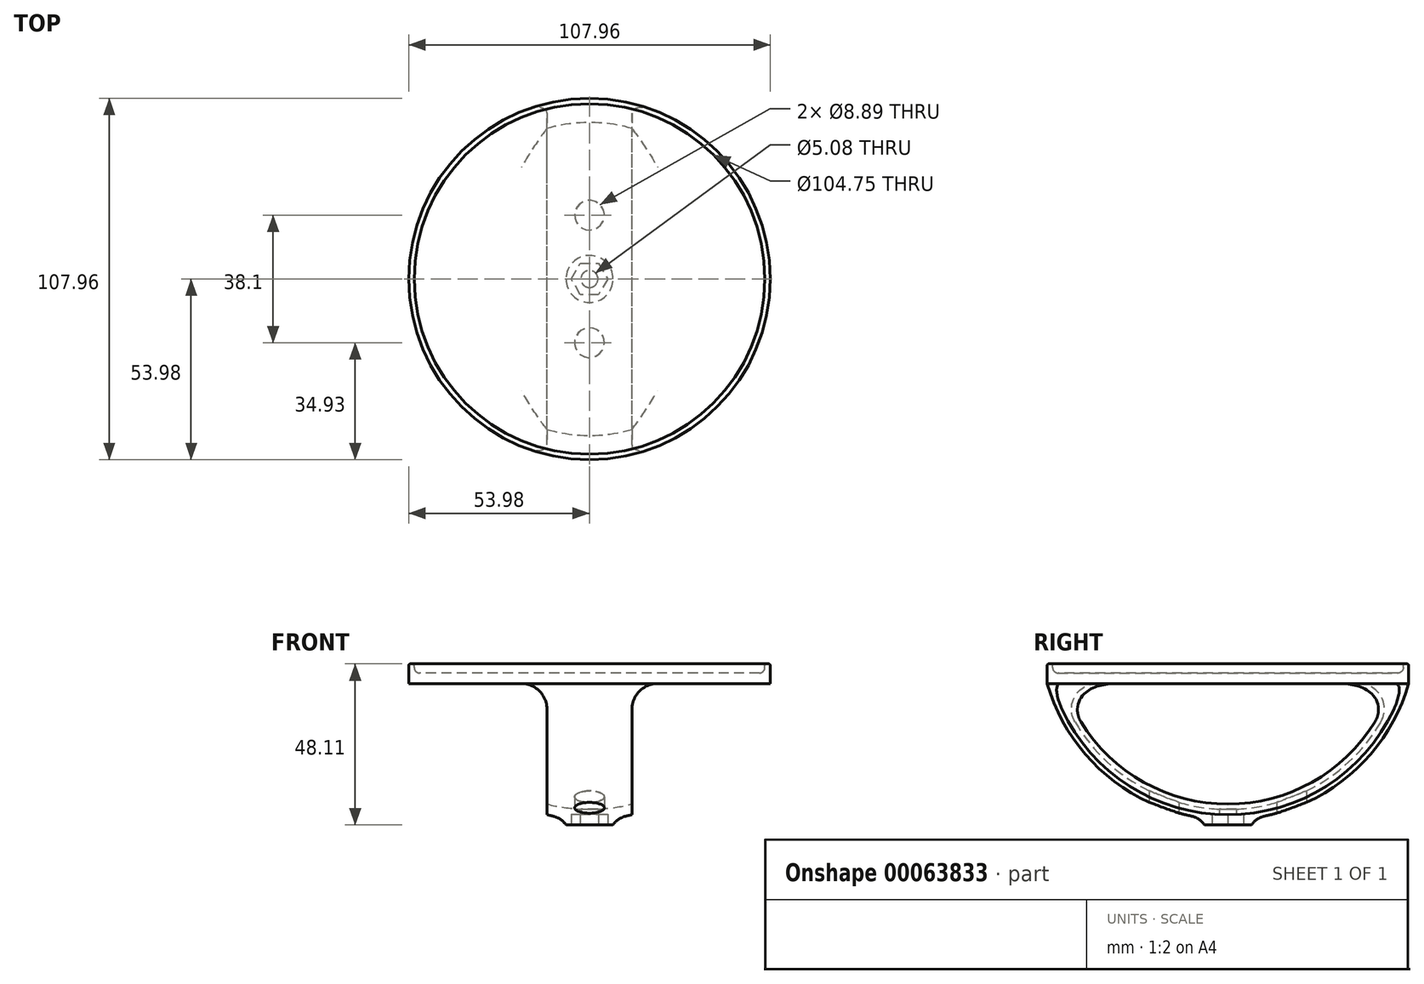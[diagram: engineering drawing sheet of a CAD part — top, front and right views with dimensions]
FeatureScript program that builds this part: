
annotation { "Feature Type Name" : "Feature", "Feature Type Description" : "" }
export const myFeature = defineFeature(function(context is Context, id is Id, definition is map)
    precondition{}
    {
        {
            var Q0;
            Q0=qCreatedBy(makeId("Front.planeOp"),FACE);
            var sketch = newSketch(context, id + "F0", { "sketchPlane" : qUnion([Q0])});
            skLineSegment(sketch, "E0", {"start": v(0, 0) * mm, "end": v(-50.74, 0) * mm});
            skLineSegment(sketch, "E1", {"start": v(-50.77, 3.17) * mm, "end": v(0, 3.17) * mm});
            skLineSegment(sketch, "E2", {"start": v(0, 0) * mm, "end": v(0, 3.17) * mm});
            skLineSegment(sketch, "E3", {"start": v(0, 3.17) * mm, "end": v(0, -13.72) * mm, "construction": true});
            skLineSegment(sketch, "E4", {"start": v(-53.98, 0) * mm, "end": v(-53.98, 5.4) * mm});
            skLineSegment(sketch, "E5", {"start": v(-53.47, 5.9) * mm, "end": v(-52.88, 5.9) * mm});
            skLineSegment(sketch, "E6", {"start": v(-52.37, 5.4) * mm, "end": v(-52.37, 4.78) * mm});
            skPoint(sketch, "E7.visualSharp", {"position": v(-52.37, 3.17) * mm});
            skArc(sketch, "E7.filletArc", {"start": v(-52.37, 4.78) * mm, "mid": v(-51.9, 3.64) * mm, "end": v(-50.77, 3.17) * mm});
            skPoint(sketch, "E8.visualSharp", {"position": v(-53.98, 5.9) * mm});
            skArc(sketch, "E8.filletArc", {"start": v(-53.47, 5.9) * mm, "mid": v(-53.83, 5.76) * mm, "end": v(-53.98, 5.4) * mm});
            skPoint(sketch, "E9.visualSharp", {"position": v(-52.37, 5.9) * mm});
            skArc(sketch, "E9.filletArc", {"start": v(-52.37, 5.4) * mm, "mid": v(-52.52, 5.76) * mm, "end": v(-52.88, 5.9) * mm});
            skArc(sketch, "E10", {"start": v(-53.97, 0) * mm, "mid": v(-33.78, -29.34) * mm, "end": v(0, -40.64) * mm});
            skArc(sketch, "E11", {"start": v(-50.74, 0) * mm, "mid": v(-31.56, -27.14) * mm, "end": v(0, -37.54) * mm});
            skLineSegment(sketch, "E12", {"start": v(0, -40.64) * mm, "end": v(0, -37.54) * mm});
            skSolve(sketch);
        }
        {
            var Q0;
            Q0=qSketchRegion(id+"F0",true);
            var Q1;
            Q1=sQuery(id+"F0.wireOp",EDGE,"E3");
            revolve(context, id + "F1", {"entities" : qUnion([Q0]), "axis" : qUnion([Q1]), "revolveType" : RevolveType.FULL});
        }
        {
            var Q0;
            Q0=qCreatedBy(makeId("Top.planeOp"),FACE);
            cPlane(context, id + "F2", {"entities" : qUnion([Q0]), "cplaneType" : CPlaneType.OFFSET, "offset" : 40.64 * mm, "oppositeDirection" : true, "width" : 152.4 * mm, "height" : 152.4 * mm});
        }
        {
            var Q0;
            Q0=qCreatedBy(id+"F2.planeOp",FACE);
            var sketch = newSketch(context, id + "F3", { "sketchPlane" : qUnion([Q0])});
            skLineSegment(sketch, "E13", {"start": v(-12.7, 65.77) * mm, "end": v(-12.7, -65.77) * mm});
            skArc(sketch, "E14", {"start": v(-12.7, 65.77) * mm, "mid": v(-66.99, 0) * mm, "end": v(-12.7, -65.77) * mm});
            skLineSegment(sketch, "E15", {"start": v(12.7, 65.77) * mm, "end": v(12.7, -65.77) * mm});
            skArc(sketch, "E16", {"start": v(12.7, -65.77) * mm, "mid": v(66.99, 0) * mm, "end": v(12.7, 65.77) * mm});
            skLineSegment(sketch, "E17", {"start": v(-12.7, 65.77) * mm, "end": v(12.7, 65.77) * mm, "construction": true});
            skPoint(sketch, "E18", {"position": v(0, 65.77) * mm});
            skCircle(sketch, "E19", {"center": v(0, 0) * mm, "radius": 2.54 * mm});
            skCircle(sketch, "E20", {"center": v(0, 19.05) * mm, "radius": 4.44 * mm});
            skCircle(sketch, "E21", {"center": v(0, -19.05) * mm, "radius": 4.44 * mm});
            skLineSegment(sketch, "E22", {"start": v(0, 0) * mm, "end": v(0, 19.05) * mm, "construction": true});
            skLineSegment(sketch, "E23", {"start": v(0, -19.05) * mm, "end": v(0, 0) * mm, "construction": true});
            skSolve(sketch);
        }
        {
            var Q0;
            Q0 = qSketchRegion(id + "F3", true);
            extrude(context, id + "F4", {"entities" : qUnion([Q0]), "operationType" : NewBodyOperationType.REMOVE, "depth" : 40.64 * mm, "offsetDistance" : 25.4 * mm});
        }
        {
            var Q0;
            Q0=makeQuery(id+"F4.boolean.opBoolean","SPLIT",EDGE,{"disambiguationData":[OD(1.0)],"derivedFrom":makeQuery(id+"F1.opRevolve","SWEPT_EDGE",EDGE,{"disambiguationData":[OSD([sQuery(id+"F0.wireOp",EDGE,"E0"),sQuery(id+"F0.wireOp",EDGE,"kr2LSTEV-fTZY-p24n-umUw-qz48NXy9PW6Q")])]})});
            var Q1;
            Q1=makeQuery(id+"F4.boolean.opBoolean","COPY",EDGE,{"disambiguationData":[OD(1.0)],"derivedFrom":makeQuery(id+"F4.opExtrude","CAP_EDGE",EDGE,{"disambiguationData":[OSD([sQuery(id+"F3.wireOp",EDGE,"E15")])],"isStart":false})});
            var Q2;
            Q2=makeQuery(id+"F4.boolean.opBoolean","COPY",EDGE,{"disambiguationData":[OD(1.0)],"derivedFrom":makeQuery(id+"F4.opExtrude","CAP_EDGE",EDGE,{"disambiguationData":[OSD([sQuery(id+"F3.wireOp",EDGE,"E13")])],"isStart":false})});
            var Q3;
            Q3=makeQuery(id+"F4.boolean.opBoolean","COPY",EDGE,{"disambiguationData":[OD(0.0)],"derivedFrom":makeQuery(id+"F4.opExtrude","CAP_EDGE",EDGE,{"disambiguationData":[OSD([sQuery(id+"F3.wireOp",EDGE,"E13")])],"isStart":false})});
            var Q4;
            Q4=makeQuery(id+"F4.boolean.opBoolean","SPLIT",EDGE,{"disambiguationData":[OD(0.0)],"derivedFrom":makeQuery(id+"F1.opRevolve","SWEPT_EDGE",EDGE,{"disambiguationData":[OSD([sQuery(id+"F0.wireOp",EDGE,"E0"),sQuery(id+"F0.wireOp",EDGE,"kr2LSTEV-fTZY-p24n-umUw-qz48NXy9PW6Q")])]})});
            var Q5;
            Q5=makeQuery(id+"F4.boolean.opBoolean","COPY",EDGE,{"disambiguationData":[OD(0.0)],"derivedFrom":makeQuery(id+"F4.opExtrude","CAP_EDGE",EDGE,{"disambiguationData":[OSD([sQuery(id+"F3.wireOp",EDGE,"E15")])],"isStart":false})});
            fillet(context, id + "F5", {"entities" : qUnion([Q0, Q1, Q2, Q3, Q4, Q5]), "radius" : 7.62 * mm, "tangentPropagation" : true, "allowEdgeOverflow" : false});
        }
        {
            var Q0;
            Q0=qCreatedBy(id+"F2.planeOp",FACE);
            var sketch = newSketch(context, id + "F6", { "sketchPlane" : qUnion([Q0])});
            skCircle(sketch, "E24.cCircle", {"center": v(0, 0) * mm, "radius": 4.7 * mm, "construction": true});
            skLineSegment(sketch, "E24.0", {"start": v(2.71, 4.7) * mm, "end": v(5.43, 0) * mm});
            skLineSegment(sketch, "E24.1", {"start": v(5.43, 0) * mm, "end": v(2.71, -4.7) * mm});
            skLineSegment(sketch, "E24.2", {"start": v(2.71, -4.7) * mm, "end": v(-2.71, -4.7) * mm});
            skLineSegment(sketch, "E24.3", {"start": v(-2.71, -4.7) * mm, "end": v(-5.43, 0) * mm});
            skLineSegment(sketch, "E24.4", {"start": v(-5.43, 0) * mm, "end": v(-2.71, 4.7) * mm});
            skLineSegment(sketch, "E24.5", {"start": v(-2.71, 4.7) * mm, "end": v(2.71, 4.7) * mm});
            skPoint(sketch, "E24.0.midPoint", {"position": v(4.07, 2.35) * mm});
            skSolve(sketch);
        }
        {
            var Q0;
            Q0 = qSketchRegion(id + "F6", true);
            extrude(context, id + "F7", {"entities" : qUnion([Q0]), "operationType" : NewBodyOperationType.REMOVE, "depth" : 1.6 * mm, "offsetDistance" : 25.4 * mm});
        }
        {
            var Q0;
            Q0=makeQuery(id+"F7.boolean.opBoolean","COPY",FACE,{"derivedFrom":makeQuery(id+"F7.opExtrude","CAP_FACE",FACE,{"disambiguationData":[OSD([sQuery(id+"F6.wireOp",EDGE,"E24.0"),sQuery(id+"F6.wireOp",EDGE,"E24.1"),sQuery(id+"F6.wireOp",EDGE,"E24.2"),sQuery(id+"F6.wireOp",EDGE,"E24.3"),sQuery(id+"F6.wireOp",EDGE,"E24.4"),sQuery(id+"F6.wireOp",EDGE,"E24.5")])],"isStart":false})});
            var sketch = newSketch(context, id + "F8", { "sketchPlane" : qUnion([Q0])});
            skCircle(sketch, "E25.cCircle", {"center": v(0, 0) * mm, "radius": 4.7 * mm, "construction": true});
            skLineSegment(sketch, "E25.0", {"start": v(5.43, 0) * mm, "end": v(2.71, -4.7) * mm});
            skLineSegment(sketch, "E25.1", {"start": v(2.71, -4.7) * mm, "end": v(-2.71, -4.7) * mm});
            skLineSegment(sketch, "E25.2", {"start": v(-2.71, -4.7) * mm, "end": v(-5.43, 0) * mm});
            skLineSegment(sketch, "E25.3", {"start": v(-5.43, 0) * mm, "end": v(-2.71, 4.7) * mm});
            skLineSegment(sketch, "E25.4", {"start": v(-2.71, 4.7) * mm, "end": v(2.71, 4.7) * mm});
            skLineSegment(sketch, "E25.5", {"start": v(2.71, 4.7) * mm, "end": v(5.43, 0) * mm});
            skPoint(sketch, "E25.0.midPoint", {"position": v(4.07, -2.35) * mm});
            skCircle(sketch, "E26", {"center": v(0, 0) * mm, "radius": 7.03 * mm});
            skSolve(sketch);
        }
        {
            var Q0;
            Q0 = qSketchRegion(id + "F8", true);
            extrude(context, id + "F9", {"entities" : qUnion([Q0]), "operationType" : NewBodyOperationType.ADD, "depth" : 3.17 * mm, "offsetDistance" : 25.4 * mm});
        }
        {
            var Q0;
            Q0=makeQuery(id+"F9.boolean.opBoolean","INTERSECT",EDGE,{"derivedFrom":[makeQuery(id+"F1.opRevolve","SWEPT_FACE",FACE,{"disambiguationData":[OSD([sQuery(id+"F0.wireOp",EDGE,"E10")])]}),makeQuery(id+"F9.opExtrude","SWEPT_FACE",FACE,{"disambiguationData":[OSD([sQuery(id+"F8.wireOp",EDGE,"E26")])]})]});
            fillet(context, id + "F10", {"entities" : qUnion([Q0]), "radius" : 6.35 * mm, "tangentPropagation" : true, "allowEdgeOverflow" : false});
        }
    });
